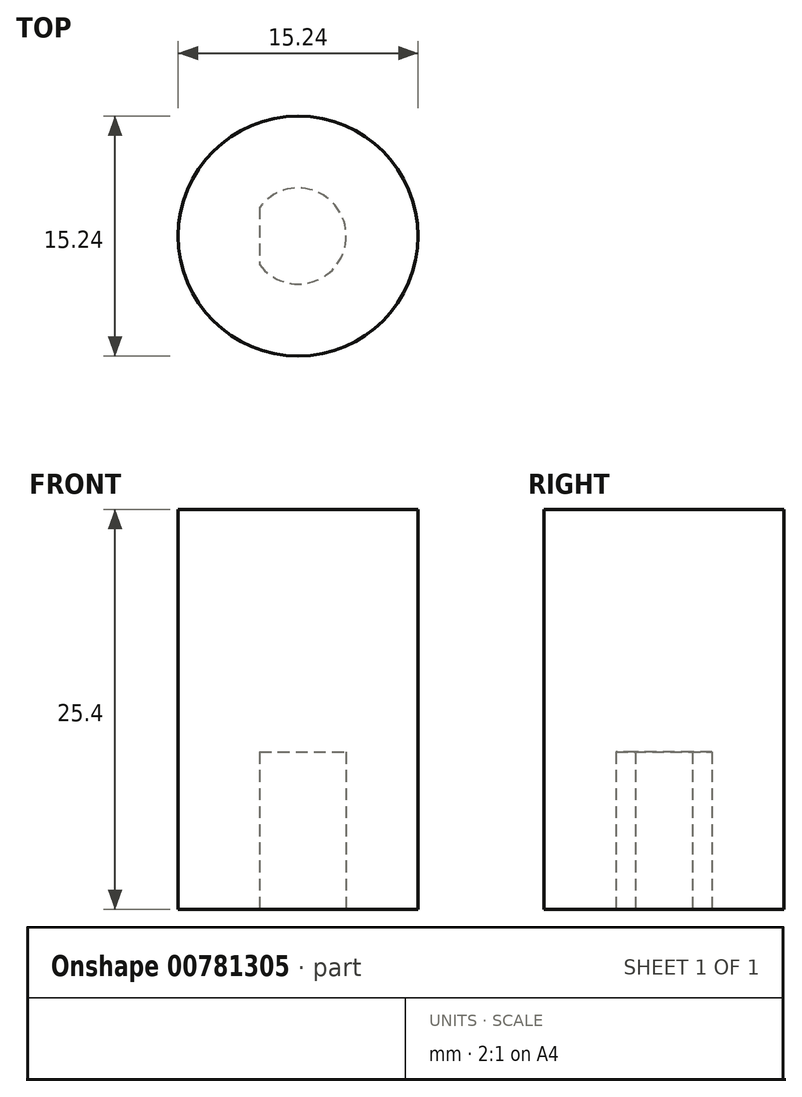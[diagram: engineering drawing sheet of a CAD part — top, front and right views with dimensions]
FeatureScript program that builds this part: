
annotation { "Feature Type Name" : "Feature", "Feature Type Description" : "" }
export const myFeature = defineFeature(function(context is Context, id is Id, definition is map)
    precondition{}
    {
        {
            var Q0;
            Q0=qCreatedBy(makeId("Top.planeOp"),FACE);
            var sketch = newSketch(context, id + "F0", { "sketchPlane" : qUnion([Q0])});
            skArc(sketch, "E0", {"start": v(-2.45, -1.82) * mm, "mid": v(3.05, 0) * mm, "end": v(-2.45, 1.82) * mm});
            skLineSegment(sketch, "E1", {"start": v(-2.45, 1.82) * mm, "end": v(-2.45, -1.82) * mm});
            skLineSegment(sketch, "E2", {"start": v(3.05, 0) * mm, "end": v(-3.05, 0) * mm, "construction": true});
            skSolve(sketch);
        }
        {
            var Q0;
            Q0=qCreatedBy(makeId("Top.planeOp"),FACE);
            var sketch = newSketch(context, id + "F1", { "sketchPlane" : qUnion([Q0])});
            skCircle(sketch, "E3", {"center": v(0, 0) * mm, "radius": 7.62 * mm});
            skSolve(sketch);
        }
        {
            var Q0;
            Q0=makeQuery(id+"F1.imprint","IMPRINT",FACE,{"disambiguationData":[TD([[makeQuery(id+"F1.imprint","IMPRINT",EDGE,{"derivedFrom":sQuery(id+"F1.wireOp",EDGE,"E3")}),1.0]])]});
            extrude(context, id + "F2", {"entities" : qUnion([Q0]), "depth" : 25.4 * mm, "offsetDistance" : 25.4 * mm});
        }
        {
            var Q0;
            Q0 = qSketchRegion(id + "F0", true);
            extrude(context, id + "F3", {"entities" : qUnion([Q0]), "operationType" : NewBodyOperationType.REMOVE, "depth" : 10 * mm, "offsetDistance" : 25.4 * mm});
        }
    });
